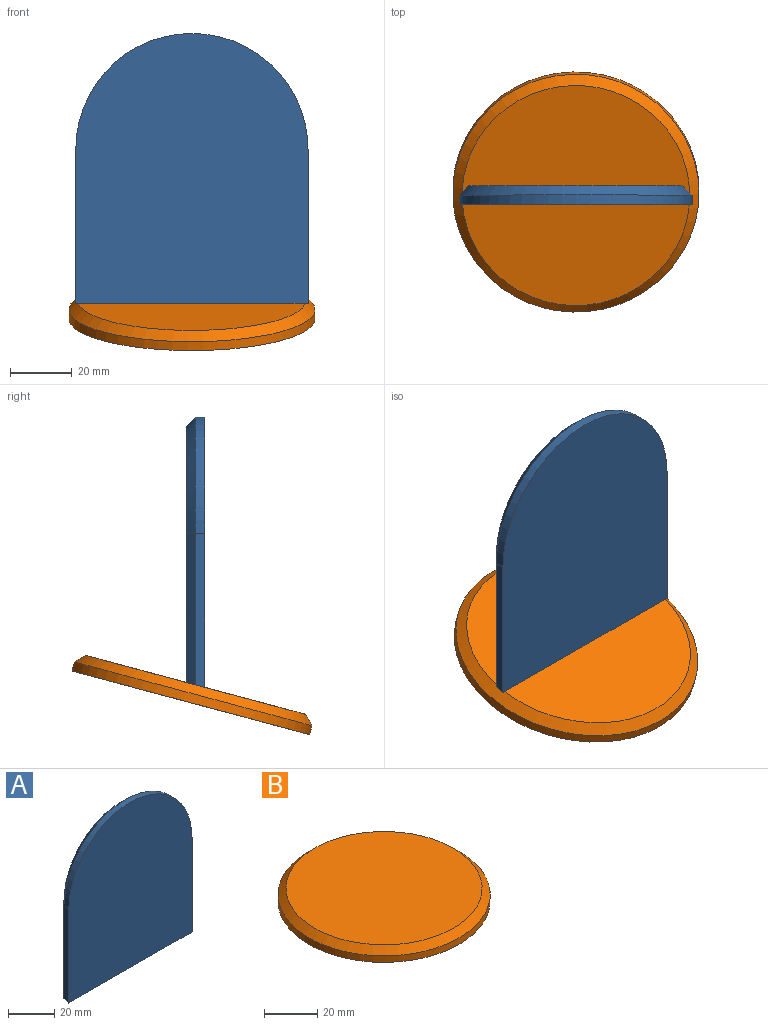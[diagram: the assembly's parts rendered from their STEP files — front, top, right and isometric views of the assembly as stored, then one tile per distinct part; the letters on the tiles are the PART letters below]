
ASSEMBLY  parts=2 mates=1
PART A: 9 faces, bbox 75.5x6x87.8 mm
  f0: cylinder r=37.75mm len=75.5mm, axis (0,1,0), area 355.8mm2, adj f1,f2,f3,f6
  f1: plane 50x3mm, normal (-1,0,0), area 148.8mm2, adj f0,f3,f5,f8
  f2: plane 50x3mm, normal (1,0,0), area 148.8mm2, adj f0,f3,f7,f8
  f3: plane 87.75x75.5mm, normal (0,-1,0), area 6013.5mm2, adj f0,f1,f2,f8
  f4: plane 83.14x69.5mm, normal (0,1,0), area 5260.1mm2, adj f5,f6,f7,f8
  f5: plane 49.2x3mm, normal (-0.71,0.71,0), area 207mm2, adj f1,f4,f6,f8
  f6: cone r=37.75mm half-angle=45deg, axis (0,-1,0), area 483.2mm2, adj f0,f4,f5,f7
  f7: plane 49.2x3mm, normal (0.71,0.71,0), area 207mm2, adj f2,f4,f6,f8
  f8: plane 75.5x6mm, normal (0,0.26,-0.97), area 459.7mm2, adj f1,f2,f3,f4,f5,f7
PART B: 4 faces, bbox 80x80x6 mm
  f0: cylinder r=40mm len=80mm, axis (0,0,-1), area 754mm2, adj f2,f3
  f1: plane 74x74mm, normal (0,0,1), area 4300.8mm2, adj f3
  f2: plane 80x80mm, normal (0,0,-1), area 5026.5mm2, adj f0
  f3: cone r=37mm half-angle=45deg, axis (0,0,-1), area 1026.3mm2, adj f0,f1
PLACE A t=(-39.96,29.5,78.85)mm
PLACE B rot(axis=(1,0,0),15deg) t=(-39.96,28.01,23.85)mm
MATE fastened B.f0 <-> A.f8  axis (0,-0.26,0.97) through (-39.96,26.46,29.65)mm
